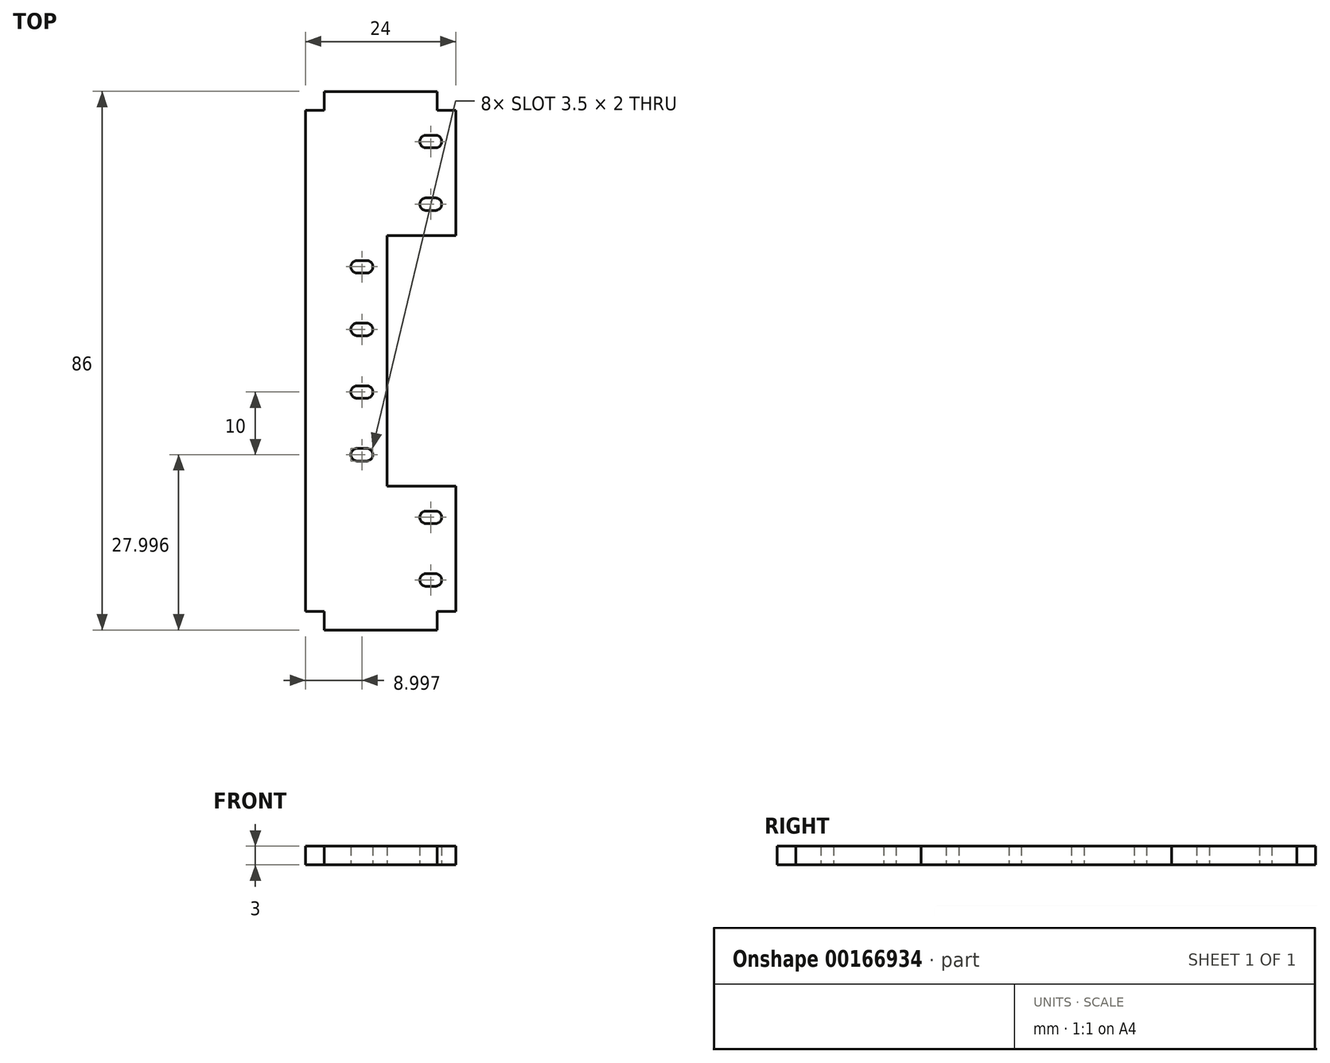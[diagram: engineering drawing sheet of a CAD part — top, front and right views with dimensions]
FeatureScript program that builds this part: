
annotation { "Feature Type Name" : "Feature", "Feature Type Description" : "" }
export const myFeature = defineFeature(function(context is Context, id is Id, definition is map)
    precondition{}
    {
        {
            var Q0;
            Q0=qCreatedBy(makeId("Top.planeOp"),FACE);
            var sketch = newSketch(context, id + "F0", { "sketchPlane" : qUnion([Q0])});
            skLineSegment(sketch, "E0", {"start": v(-52.6, 86.28) * mm, "end": v(-55.6, 86.28) * mm});
            skLineSegment(sketch, "E1", {"start": v(-55.6, 86.28) * mm, "end": v(-55.6, 6.28) * mm});
            skLineSegment(sketch, "E2", {"start": v(-55.6, 6.28) * mm, "end": v(-52.6, 6.28) * mm});
            skLineSegment(sketch, "E3", {"start": v(-52.6, 6.28) * mm, "end": v(-52.6, 3.28) * mm});
            skLineSegment(sketch, "E4", {"start": v(-52.6, 3.28) * mm, "end": v(-34.6, 3.28) * mm});
            skLineSegment(sketch, "E5", {"start": v(-34.6, 3.28) * mm, "end": v(-34.6, 6.28) * mm});
            skLineSegment(sketch, "E6", {"start": v(-34.6, 6.28) * mm, "end": v(-31.6, 6.28) * mm});
            skLineSegment(sketch, "E7", {"start": v(-31.6, 6.28) * mm, "end": v(-31.6, 26.28) * mm});
            skLineSegment(sketch, "E8", {"start": v(-31.6, 26.28) * mm, "end": v(-42.6, 26.28) * mm});
            skLineSegment(sketch, "E9", {"start": v(-42.6, 26.28) * mm, "end": v(-42.6, 66.28) * mm});
            skLineSegment(sketch, "E10", {"start": v(-42.6, 66.28) * mm, "end": v(-31.6, 66.28) * mm});
            skLineSegment(sketch, "E11", {"start": v(-31.6, 66.28) * mm, "end": v(-31.6, 86.28) * mm});
            skLineSegment(sketch, "E12", {"start": v(-31.6, 86.28) * mm, "end": v(-34.6, 86.28) * mm});
            skLineSegment(sketch, "E13", {"start": v(-34.6, 86.28) * mm, "end": v(-34.6, 89.28) * mm});
            skLineSegment(sketch, "E14", {"start": v(-34.6, 89.28) * mm, "end": v(-52.6, 89.28) * mm});
            skLineSegment(sketch, "E15", {"start": v(-52.6, 89.28) * mm, "end": v(-52.6, 86.28) * mm});
            skArc(sketch, "E16", {"start": v(-37.35, 81.28) * mm, "mid": v(-37.06, 80.57) * mm, "end": v(-36.35, 80.28) * mm});
            skLineSegment(sketch, "E17", {"start": v(-36.35, 80.28) * mm, "end": v(-34.85, 80.28) * mm});
            skArc(sketch, "E18", {"start": v(-34.85, 80.28) * mm, "mid": v(-34.15, 80.57) * mm, "end": v(-33.85, 81.28) * mm});
            skArc(sketch, "E19", {"start": v(-33.85, 81.28) * mm, "mid": v(-34.15, 81.98) * mm, "end": v(-34.85, 82.28) * mm});
            skLineSegment(sketch, "E20", {"start": v(-34.85, 82.28) * mm, "end": v(-36.35, 82.28) * mm});
            skArc(sketch, "E21", {"start": v(-36.35, 82.28) * mm, "mid": v(-37.06, 81.98) * mm, "end": v(-37.35, 81.28) * mm});
            skArc(sketch, "E22", {"start": v(-37.35, 71.28) * mm, "mid": v(-37.06, 70.57) * mm, "end": v(-36.35, 70.28) * mm});
            skLineSegment(sketch, "E23", {"start": v(-36.35, 70.28) * mm, "end": v(-34.85, 70.28) * mm});
            skArc(sketch, "E24", {"start": v(-34.85, 70.28) * mm, "mid": v(-34.15, 70.57) * mm, "end": v(-33.85, 71.28) * mm});
            skArc(sketch, "E25", {"start": v(-33.85, 71.28) * mm, "mid": v(-34.15, 71.98) * mm, "end": v(-34.85, 72.28) * mm});
            skLineSegment(sketch, "E26", {"start": v(-34.85, 72.28) * mm, "end": v(-36.35, 72.28) * mm});
            skArc(sketch, "E27", {"start": v(-36.35, 72.28) * mm, "mid": v(-37.06, 71.98) * mm, "end": v(-37.35, 71.28) * mm});
            skArc(sketch, "E28", {"start": v(-48.35, 61.28) * mm, "mid": v(-48.06, 60.57) * mm, "end": v(-47.35, 60.28) * mm});
            skLineSegment(sketch, "E29", {"start": v(-47.35, 60.28) * mm, "end": v(-45.85, 60.28) * mm});
            skArc(sketch, "E30", {"start": v(-45.85, 60.28) * mm, "mid": v(-45.15, 60.57) * mm, "end": v(-44.85, 61.28) * mm});
            skArc(sketch, "E31", {"start": v(-44.85, 61.28) * mm, "mid": v(-45.15, 61.98) * mm, "end": v(-45.85, 62.28) * mm});
            skLineSegment(sketch, "E32", {"start": v(-45.85, 62.28) * mm, "end": v(-47.35, 62.28) * mm});
            skArc(sketch, "E33", {"start": v(-47.35, 62.28) * mm, "mid": v(-48.06, 61.98) * mm, "end": v(-48.35, 61.28) * mm});
            skArc(sketch, "E34", {"start": v(-48.35, 51.28) * mm, "mid": v(-48.06, 50.57) * mm, "end": v(-47.35, 50.28) * mm});
            skLineSegment(sketch, "E35", {"start": v(-47.35, 50.28) * mm, "end": v(-45.85, 50.28) * mm});
            skArc(sketch, "E36", {"start": v(-45.85, 50.28) * mm, "mid": v(-45.15, 50.57) * mm, "end": v(-44.85, 51.28) * mm});
            skArc(sketch, "E37", {"start": v(-44.85, 51.28) * mm, "mid": v(-45.15, 51.98) * mm, "end": v(-45.85, 52.28) * mm});
            skLineSegment(sketch, "E38", {"start": v(-45.85, 52.28) * mm, "end": v(-47.35, 52.28) * mm});
            skArc(sketch, "E39", {"start": v(-47.35, 52.28) * mm, "mid": v(-48.06, 51.98) * mm, "end": v(-48.35, 51.28) * mm});
            skArc(sketch, "E40", {"start": v(-48.35, 41.28) * mm, "mid": v(-48.06, 40.57) * mm, "end": v(-47.35, 40.28) * mm});
            skLineSegment(sketch, "E41", {"start": v(-47.35, 40.28) * mm, "end": v(-45.85, 40.28) * mm});
            skArc(sketch, "E42", {"start": v(-45.85, 40.28) * mm, "mid": v(-45.15, 40.57) * mm, "end": v(-44.85, 41.28) * mm});
            skArc(sketch, "E43", {"start": v(-44.85, 41.28) * mm, "mid": v(-45.15, 41.98) * mm, "end": v(-45.85, 42.28) * mm});
            skLineSegment(sketch, "E44", {"start": v(-45.85, 42.28) * mm, "end": v(-47.35, 42.28) * mm});
            skArc(sketch, "E45", {"start": v(-47.35, 42.28) * mm, "mid": v(-48.06, 41.98) * mm, "end": v(-48.35, 41.28) * mm});
            skArc(sketch, "E46", {"start": v(-48.35, 31.28) * mm, "mid": v(-48.06, 30.57) * mm, "end": v(-47.35, 30.28) * mm});
            skLineSegment(sketch, "E47", {"start": v(-47.35, 30.28) * mm, "end": v(-45.85, 30.28) * mm});
            skArc(sketch, "E48", {"start": v(-45.85, 30.28) * mm, "mid": v(-45.15, 30.57) * mm, "end": v(-44.85, 31.28) * mm});
            skArc(sketch, "E49", {"start": v(-44.85, 31.28) * mm, "mid": v(-45.15, 31.98) * mm, "end": v(-45.85, 32.28) * mm});
            skLineSegment(sketch, "E50", {"start": v(-45.85, 32.28) * mm, "end": v(-47.35, 32.28) * mm});
            skArc(sketch, "E51", {"start": v(-47.35, 32.28) * mm, "mid": v(-48.06, 31.98) * mm, "end": v(-48.35, 31.28) * mm});
            skArc(sketch, "E52", {"start": v(-37.35, 21.28) * mm, "mid": v(-37.06, 20.57) * mm, "end": v(-36.35, 20.28) * mm});
            skLineSegment(sketch, "E53", {"start": v(-36.35, 20.28) * mm, "end": v(-34.85, 20.28) * mm});
            skArc(sketch, "E54", {"start": v(-34.85, 20.28) * mm, "mid": v(-34.15, 20.57) * mm, "end": v(-33.85, 21.28) * mm});
            skArc(sketch, "E55", {"start": v(-33.85, 21.28) * mm, "mid": v(-34.15, 21.98) * mm, "end": v(-34.85, 22.28) * mm});
            skLineSegment(sketch, "E56", {"start": v(-34.85, 22.28) * mm, "end": v(-36.35, 22.28) * mm});
            skArc(sketch, "E57", {"start": v(-36.35, 22.28) * mm, "mid": v(-37.06, 21.98) * mm, "end": v(-37.35, 21.28) * mm});
            skArc(sketch, "E58", {"start": v(-37.35, 11.28) * mm, "mid": v(-37.06, 10.57) * mm, "end": v(-36.35, 10.28) * mm});
            skLineSegment(sketch, "E59", {"start": v(-36.35, 10.28) * mm, "end": v(-34.85, 10.28) * mm});
            skArc(sketch, "E60", {"start": v(-34.85, 10.28) * mm, "mid": v(-34.15, 10.57) * mm, "end": v(-33.85, 11.28) * mm});
            skArc(sketch, "E61", {"start": v(-33.85, 11.28) * mm, "mid": v(-34.15, 11.98) * mm, "end": v(-34.85, 12.28) * mm});
            skLineSegment(sketch, "E62", {"start": v(-34.85, 12.28) * mm, "end": v(-36.35, 12.28) * mm});
            skArc(sketch, "E63", {"start": v(-36.35, 12.28) * mm, "mid": v(-37.06, 11.98) * mm, "end": v(-37.35, 11.28) * mm});
            skSolve(sketch);
        }
        {
            var Q0;
            Q0=makeQuery(id+"F0.imprint","IMPRINT",FACE,{"disambiguationData":[TD([[makeQuery(id+"F0.imprint","IMPRINT",EDGE,{"derivedFrom":sQuery(id+"F0.wireOp",EDGE,"E0")}),1.0]])]});
            extrude(context, id + "F1", {"entities" : qUnion([Q0]), "endBound" : BoundingType.SYMMETRIC, "depth" : 3 * mm});
        }
    });
